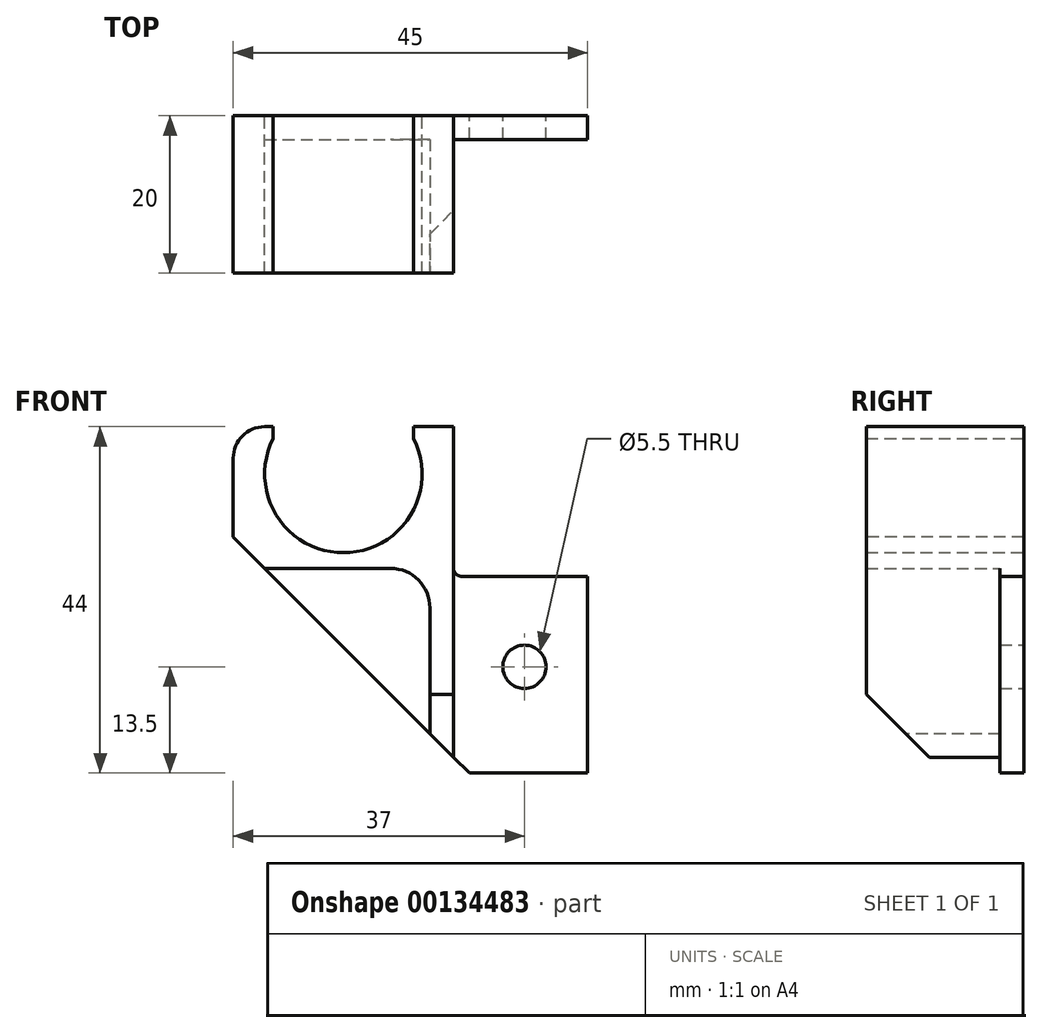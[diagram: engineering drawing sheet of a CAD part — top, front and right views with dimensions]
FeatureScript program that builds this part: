
annotation { "Feature Type Name" : "Feature", "Feature Type Description" : "" }
export const myFeature = defineFeature(function(context is Context, id is Id, definition is map)
    precondition{}
    {
        {
            var Q0;
            Q0=qCreatedBy(makeId("Front.planeOp"),FACE);
            var sketch = newSketch(context, id + "F0", { "sketchPlane" : qUnion([Q0])});
            skArc(sketch, "E0", {"start": v(-22.93, 17.5) * mm, "mid": v(-14, 3) * mm, "end": v(-5.07, 17.5) * mm});
            skLineSegment(sketch, "E1", {"start": v(-22.93, 19) * mm, "end": v(-28, 19) * mm});
            skLineSegment(sketch, "E2", {"start": v(-28, 19) * mm, "end": v(-28, -25) * mm});
            skLineSegment(sketch, "E3", {"start": v(-28, -25) * mm, "end": v(17, -25) * mm});
            skLineSegment(sketch, "E4", {"start": v(17, -25) * mm, "end": v(17, 0) * mm});
            skLineSegment(sketch, "E5", {"start": v(17, 0) * mm, "end": v(0, 0) * mm});
            skLineSegment(sketch, "E6", {"start": v(0, 0) * mm, "end": v(0, 19) * mm});
            skLineSegment(sketch, "E7", {"start": v(0, 19) * mm, "end": v(-5.07, 19) * mm});
            skLineSegment(sketch, "E8", {"start": v(-22.93, 19) * mm, "end": v(-22.93, 17.5) * mm});
            skLineSegment(sketch, "E9", {"start": v(-5.07, 19) * mm, "end": v(-5.07, 17.5) * mm});
            skCircle(sketch, "E10", {"center": v(9, -11.5) * mm, "radius": 2.75 * mm});
            skSolve(sketch);
        }
        {
            var Q0;
            Q0 = qSketchRegion(id + "F0", true);
            extrude(context, id + "F1", {"entities" : qUnion([Q0]), "depth" : 20 * mm});
        }
        {
            var Q0;
            Q0=makeQuery(id+"F1.opExtrude","SWEPT_EDGE",EDGE,{"disambiguationData":[OSD([sQuery(id+"F0.wireOp",EDGE,"E2"),sQuery(id+"F0.wireOp",EDGE,"E3")])]});
            chamfer(context, id + "F2", {"entities" : qUnion([Q0]), "width" : 30 * mm, "tangentPropagation" : true});
        }
        {
            var Q0;
            Q0=makeQuery(id+"F1.opExtrude","SWEPT_EDGE",EDGE,{"disambiguationData":[OSD([sQuery(id+"F0.wireOp",EDGE,"E5"),sQuery(id+"F0.wireOp",EDGE,"E6")])]});
            fillet(context, id + "F3", {"entities" : qUnion([Q0]), "radius" : 1 * mm, "tangentPropagation" : true, "allowEdgeOverflow" : false});
        }
        {
            var Q0;
            Q0=makeQuery(id+"F1.opExtrude","SWEPT_EDGE",EDGE,{"disambiguationData":[OSD([sQuery(id+"F0.wireOp",EDGE,"E1"),sQuery(id+"F0.wireOp",EDGE,"E2")])]});
            fillet(context, id + "F4", {"entities" : qUnion([Q0]), "radius" : 4 * mm, "tangentPropagation" : true, "allowEdgeOverflow" : false});
        }
        {
            var Q0;
            Q0=makeQuery(id+"F1.opExtrude","CAP_EDGE",EDGE,{"disambiguationData":[OSD([sQuery(id+"F0.wireOp",EDGE,"E3")])],"isStart":false});
            chamfer(context, id + "F5", {"entities" : qUnion([Q0]), "width" : 10 * mm, "tangentPropagation" : true});
        }
        {
            var Q0;
            Q0=makeQuery(id+"F1.opExtrude","CAP_FACE",FACE,{"disambiguationData":[OSD([sQuery(id+"F0.wireOp",EDGE,"E0"),sQuery(id+"F0.wireOp",EDGE,"E1"),sQuery(id+"F0.wireOp",EDGE,"E2"),sQuery(id+"F0.wireOp",EDGE,"E3"),sQuery(id+"F0.wireOp",EDGE,"E4"),sQuery(id+"F0.wireOp",EDGE,"E5"),sQuery(id+"F0.wireOp",EDGE,"E6"),sQuery(id+"F0.wireOp",EDGE,"E7"),sQuery(id+"F0.wireOp",EDGE,"E8"),sQuery(id+"F0.wireOp",EDGE,"E9")])],"isStart":false});
            var sketch = newSketch(context, id + "F6", { "sketchPlane" : qUnion([Q0])});
            skLineSegment(sketch, "E11.bottom", {"start": v(-27.3, 1) * mm, "end": v(-3, 1) * mm});
            skLineSegment(sketch, "E11.top", {"start": v(-27.3, -30.84) * mm, "end": v(-3, -30.84) * mm});
            skLineSegment(sketch, "E11.left", {"start": v(-27.3, 1) * mm, "end": v(-27.3, -30.84) * mm});
            skLineSegment(sketch, "E11.right", {"start": v(-3, 1) * mm, "end": v(-3, -30.84) * mm});
            skLineSegment(sketch, "E12.bottom", {"start": v(0, 19) * mm, "end": v(17.98, 19) * mm});
            skLineSegment(sketch, "E12.top", {"start": v(0, -30.4) * mm, "end": v(17.98, -30.4) * mm});
            skLineSegment(sketch, "E12.left", {"start": v(0, 19) * mm, "end": v(0, -30.4) * mm});
            skLineSegment(sketch, "E12.right", {"start": v(17.98, 19) * mm, "end": v(17.98, -30.4) * mm});
            skSolve(sketch);
        }
        {
            var Q0;
            Q0 = qSketchRegion(id + "F6", true);
            extrude(context, id + "F7", {"entities" : qUnion([Q0]), "operationType" : NewBodyOperationType.REMOVE, "oppositeDirection" : true, "depth" : 17 * mm});
        }
        {
            var Q0;
            Q0=makeQuery(id+"F7.boolean.opBoolean","COPY",EDGE,{"derivedFrom":makeQuery(id+"F7.opExtrude","SWEPT_EDGE",EDGE,{"disambiguationData":[OSD([sQuery(id+"F6.wireOp",EDGE,"E11.bottom"),sQuery(id+"F6.wireOp",EDGE,"E11.right")])]})});
            fillet(context, id + "F8", {"entities" : qUnion([Q0]), "radius" : 5 * mm, "tangentPropagation" : true, "allowEdgeOverflow" : false});
        }
    });
